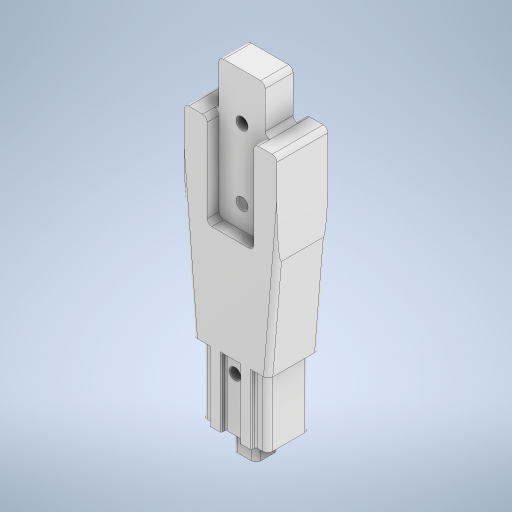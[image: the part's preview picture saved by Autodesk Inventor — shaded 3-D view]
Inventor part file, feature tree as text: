
AUTODESK INVENTOR PART (.ipt)
format: ipt  version: 2024.3 (Build 283343000, 343)  size: 538,112 bytes
history: native  units: mm
features: extrude x10, sketch x10, fillet x3, other x1, projected_geometry x1
ambient origin geometry x8: Origin, YZ Plane, XZ Plane, XY Plane, X Axis, Y Axis, Z Axis, Center Point
bodies: Body1 (feature_tree)
feature tree (25):
  other  "ソリッド1"
  extrude  "押し出し1"  Depth=40.0mm
  extrude  "押し出し2"  Depth=10.0mm
  extrude  "押し出し3"  Depth=10.0mm
  fillet  "フィレット1"  Radius=50.0mm
  extrude  "押し出し14"  Depth=10.0mm
  extrude  "押し出し15"  Depth=30.0mm
  extrude  "押し出し16"  Depth=5.2mm
  extrude  "押し出し18"  Depth=5.2mm
  extrude  "押し出し19"  Depth=20.0mm
  fillet  "フィレット5"  Radius=22.0mm
  extrude  "押し出し20"  Depth=120.0mm
  extrude  "押し出し21"  Depth=20.0mm
  fillet  "フィレット6"  Radius=50.0mm
  sketch  "スケッチ1"
  sketch  "スケッチ2"
  sketch  "スケッチ3"
  sketch  "スケッチ17"
  sketch  "スケッチ18"
  projected_geometry  "投影ループ3"
  sketch  "スケッチ19"
  sketch  "スケッチ21"
  sketch  "スケッチ22"
  sketch  "スケッチ23"
  sketch  "スケッチ24"
